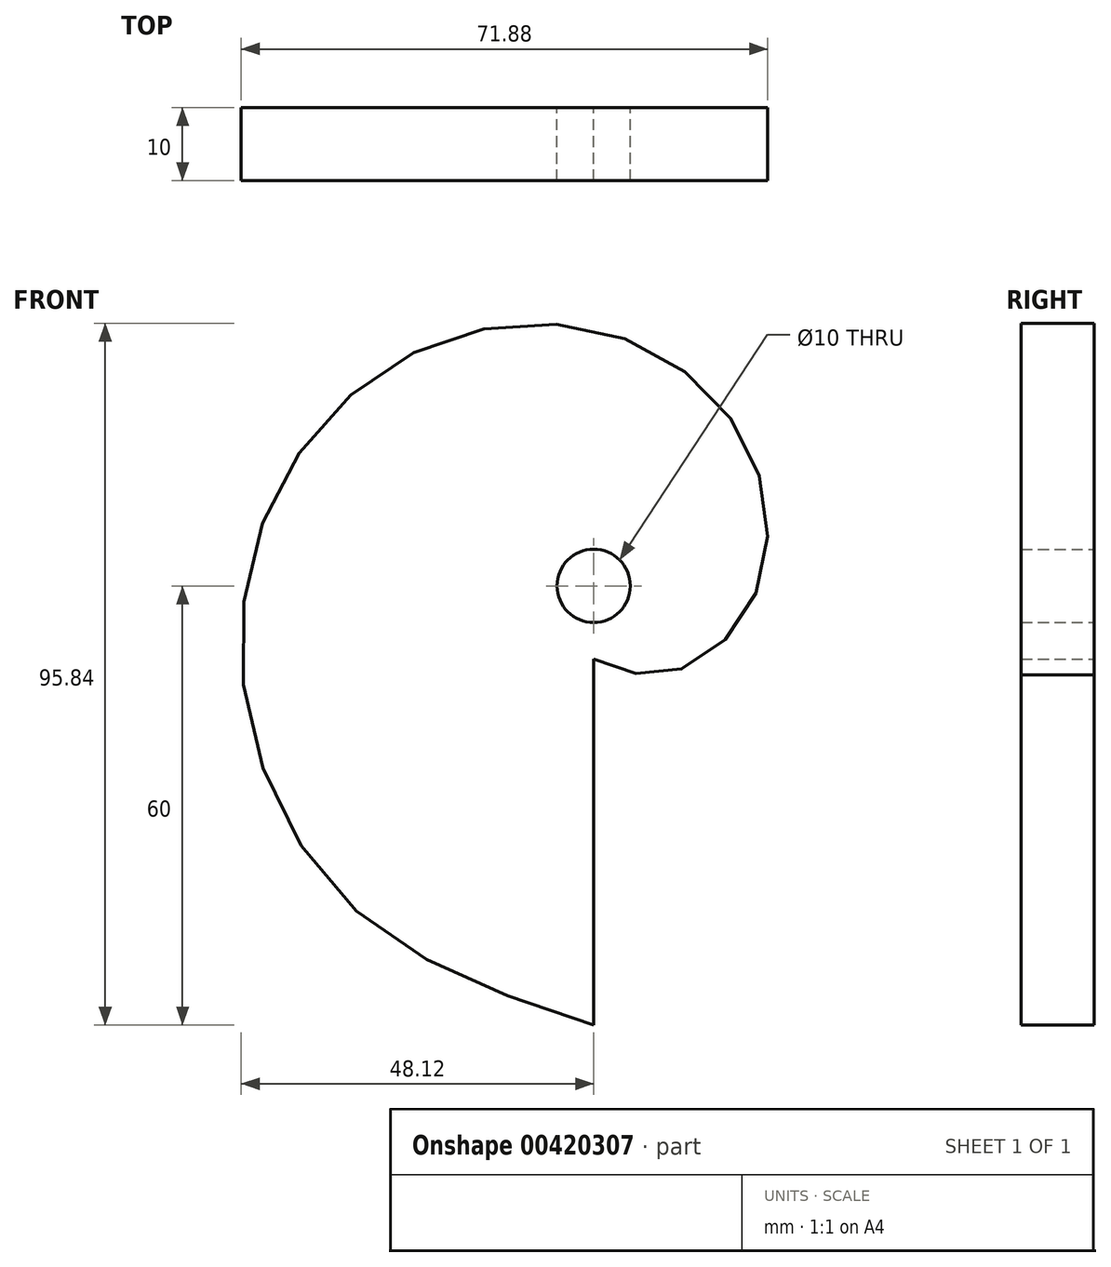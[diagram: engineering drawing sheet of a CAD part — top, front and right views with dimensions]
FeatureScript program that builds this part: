
annotation { "Feature Type Name" : "Feature", "Feature Type Description" : "" }
export const myFeature = defineFeature(function(context is Context, id is Id, definition is map)
    precondition{}
    {
        {
            var Q0;
            Q0=qCreatedBy(makeId("Front.planeOp"),FACE);
            var sketch = newSketch(context, id + "F0", { "sketchPlane" : qUnion([Q0])});
            skPoint(sketch, "E0.0.midPoint", {"position": v(-55.62, 0) * mm});
            skFitSpline(sketch, "E1", {"points": [v(0, -10) * mm, v(8.82, -12.13) * mm, v(19.02, -6.2) * mm, v(23.76, 7.77) * mm, v(17.6, 24.3) * mm, v(0, 35) * mm, v(-23.57, 32.32) * mm, v(-42.78, 13.95) * mm, v(-47.54, -15.5) * mm, v(-32.17, -44.61) * mm, v(0, -60) * mm], "startDerivative": vector(131.45, -55.72) * mm, "endDerivative": vector(273.32, -89.8) * mm});
            skLineSegment(sketch, "E2", {"start": v(0, -60) * mm, "end": v(0, -10) * mm});
            skCircle(sketch, "E3", {"center": v(0, 0) * mm, "radius": 5 * mm});
            skSolve(sketch);
        }
        {
            var Q0;
            Q0=makeQuery(id+"F0.imprint","IMPRINT",FACE,{"disambiguationData":[TD([[makeQuery(id+"F0.imprint","IMPRINT",EDGE,{"derivedFrom":sQuery(id+"F0.wireOp",EDGE,"E1")}),1.0]])]});
            extrude(context, id + "F1", {"entities" : qUnion([Q0]), "depth" : 10 * mm, "offsetDistance" : 25 * mm});
        }
    });
